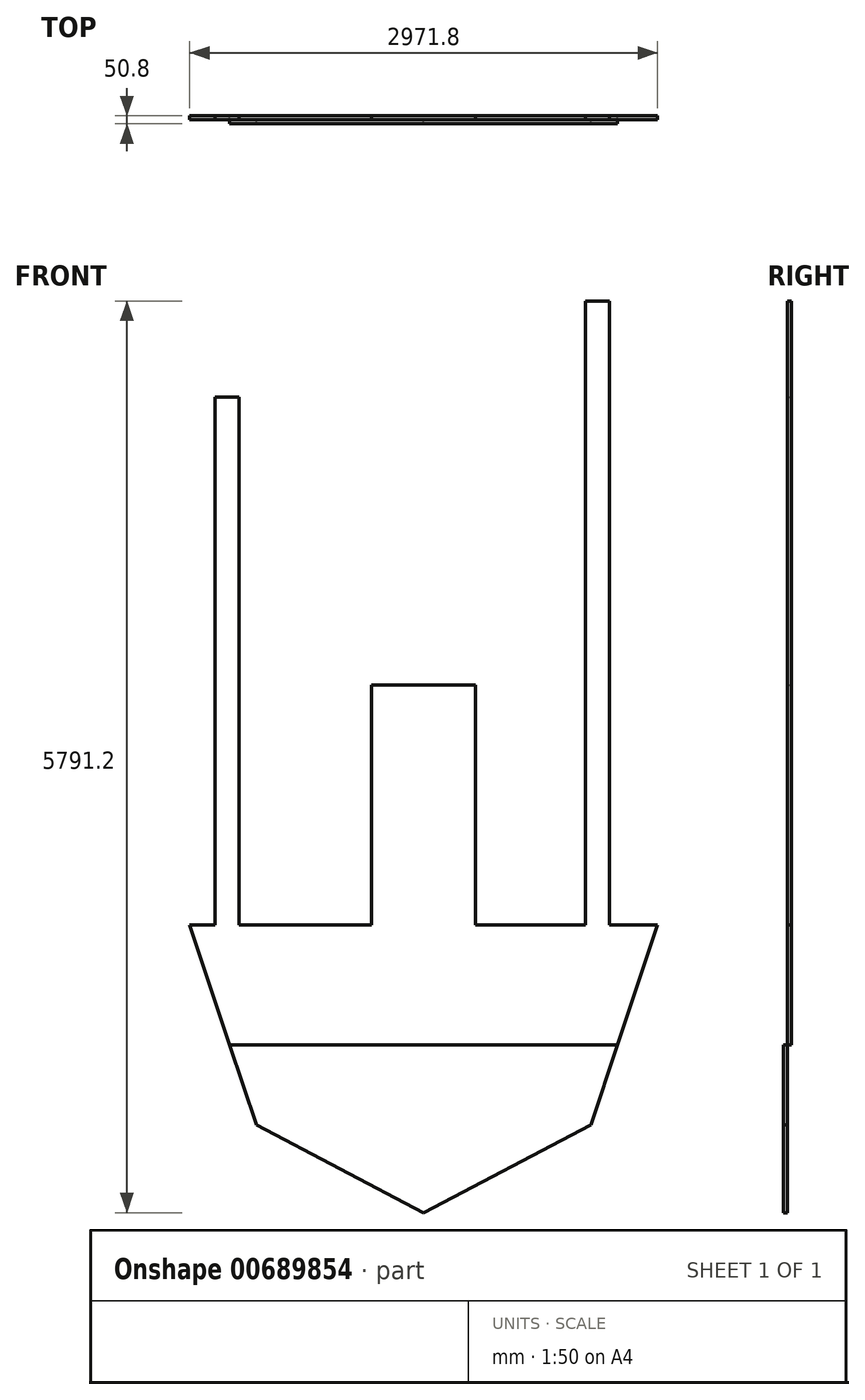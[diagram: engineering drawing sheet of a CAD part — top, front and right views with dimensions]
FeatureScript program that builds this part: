
annotation { "Feature Type Name" : "Feature", "Feature Type Description" : "" }
export const myFeature = defineFeature(function(context is Context, id is Id, definition is map)
    precondition{}
    {
        {
            var Q0;
            Q0=qCreatedBy(makeId("Front.planeOp"),FACE);
            var sketch = newSketch(context, id + "F0", { "sketchPlane" : qUnion([Q0])});
            skLineSegment(sketch, "E0", {"start": v(-1485.9, 762) * mm, "end": v(-1324.84, 762) * mm});
            skLineSegment(sketch, "E1", {"start": v(1485.9, 762) * mm, "end": v(1231.9, 0) * mm});
            skLineSegment(sketch, "E2", {"start": v(1231.9, 0) * mm, "end": v(-1231.9, 0) * mm});
            skLineSegment(sketch, "E3", {"start": v(-1231.9, 0) * mm, "end": v(-1485.9, 762) * mm});
            skLineSegment(sketch, "E4", {"start": v(0, 0) * mm, "end": v(0, 762) * mm, "construction": true});
            skLineSegment(sketch, "E5.top", {"start": v(-330.2, 2286) * mm, "end": v(330.2, 2286) * mm});
            skLineSegment(sketch, "E5.left", {"start": v(-330.2, 762) * mm, "end": v(-330.2, 2286) * mm});
            skLineSegment(sketch, "E5.right", {"start": v(330.2, 762) * mm, "end": v(330.2, 2286) * mm});
            skLineSegment(sketch, "E6", {"start": v(0, 0) * mm, "end": v(0, 2286) * mm, "construction": true});
            skLineSegment(sketch, "E7.trimOffspring", {"start": v(330.2, 762) * mm, "end": v(1027.54, 762) * mm});
            skLineSegment(sketch, "E8.top", {"start": v(-1324.84, 4114.8) * mm, "end": v(-1172.44, 4114.8) * mm});
            skLineSegment(sketch, "E8.left", {"start": v(-1324.84, 762) * mm, "end": v(-1324.84, 4114.8) * mm});
            skLineSegment(sketch, "E8.right", {"start": v(-1172.44, 762) * mm, "end": v(-1172.44, 4114.8) * mm});
            skLineSegment(sketch, "E9.top", {"start": v(1027.54, 4724.4) * mm, "end": v(1179.94, 4724.4) * mm});
            skLineSegment(sketch, "E9.left", {"start": v(1027.54, 762) * mm, "end": v(1027.54, 4724.4) * mm});
            skLineSegment(sketch, "E9.right", {"start": v(1179.94, 762) * mm, "end": v(1179.94, 4724.4) * mm});
            skLineSegment(sketch, "E10.trimOffspring", {"start": v(1179.94, 762) * mm, "end": v(1485.9, 762) * mm});
            skLineSegment(sketch, "E11.trimOffspring", {"start": v(-1172.44, 762) * mm, "end": v(-330.2, 762) * mm});
            skSolve(sketch);
        }
        {
            var Q0;
            Q0 = qSketchRegion(id + "F0", true);
            extrude(context, id + "F1", {"entities" : qUnion([Q0]), "depth" : 25.4 * mm, "offsetDistance" : 25.4 * mm});
        }
        {
            var Q0;
            Q0=makeQuery(id+"F1.opExtrude","CAP_FACE",FACE,{"disambiguationData":[OSD([sQuery(id+"F0.wireOp",EDGE,"E0"),sQuery(id+"F0.wireOp",EDGE,"E1"),sQuery(id+"F0.wireOp",EDGE,"E2"),sQuery(id+"F0.wireOp",EDGE,"E3"),sQuery(id+"F0.wireOp",EDGE,"E5.top"),sQuery(id+"F0.wireOp",EDGE,"E5.left"),sQuery(id+"F0.wireOp",EDGE,"E5.right"),sQuery(id+"F0.wireOp",EDGE,"E7.trimOffspring"),sQuery(id+"F0.wireOp",EDGE,"E8.top"),sQuery(id+"F0.wireOp",EDGE,"E8.left"),sQuery(id+"F0.wireOp",EDGE,"E8.right"),sQuery(id+"F0.wireOp",EDGE,"E9.top"),sQuery(id+"F0.wireOp",EDGE,"E9.left"),sQuery(id+"F0.wireOp",EDGE,"E9.right"),sQuery(id+"F0.wireOp",EDGE,"E10.trimOffspring"),sQuery(id+"F0.wireOp",EDGE,"E11.trimOffspring")])],"isStart":false});
            var sketch = newSketch(context, id + "F2", { "sketchPlane" : qUnion([Q0])});
            skLineSegment(sketch, "E12", {"start": v(-1231.9, 0) * mm, "end": v(-1062.57, -508) * mm});
            skLineSegment(sketch, "E13", {"start": v(-1062.57, -508) * mm, "end": v(0, -1066.8) * mm});
            skLineSegment(sketch, "E14", {"start": v(0, -1066.8) * mm, "end": v(1062.57, -508) * mm});
            skLineSegment(sketch, "E15", {"start": v(1062.57, -508) * mm, "end": v(1231.9, 0) * mm});
            skLineSegment(sketch, "E16", {"start": v(1231.9, 0) * mm, "end": v(-1231.9, 0) * mm});
            skSolve(sketch);
        }
        {
            var Q0;
            Q0 = qSketchRegion(id + "F2", true);
            extrude(context, id + "F3", {"entities" : qUnion([Q0]), "depth" : 25.4 * mm, "offsetDistance" : 25.4 * mm});
        }
    });
